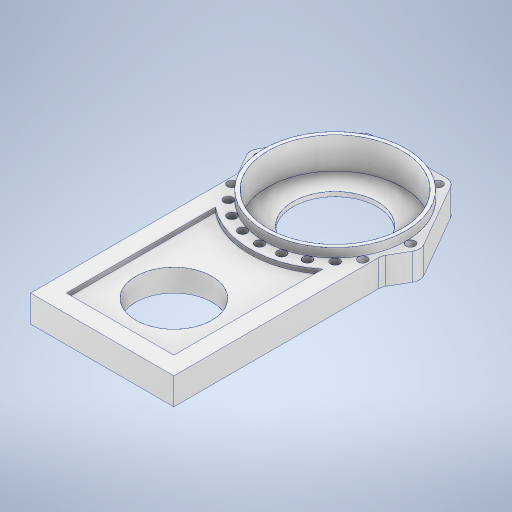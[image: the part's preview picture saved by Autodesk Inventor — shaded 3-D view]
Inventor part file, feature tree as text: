
AUTODESK INVENTOR PART (.ipt)
format: ipt  version: 2024 (Build 280153000, 153)  size: 427,520 bytes
history: native  units: mm
features: extrude x9, sketch x9, fillet x1, projected_geometry x1
ambient origin geometry x8: Origin, YZ Plane, XZ Plane, XY Plane, X Axis, Y Axis, Z Axis, Center Point
bodies: Solid1 (feature_tree)
feature tree (20):
  extrude  "Extrusion1"  Depth=160.0mm
  extrude  "Extrusion2"  Depth=30.0mm TaperAngle=0.0deg
  sketch  "Sketch3"  dims[d5=150.0mm d6=40.0mm d7=0.0mm]
  extrude  "Extrusion3"  Depth=40.0mm TaperAngle=0.0deg
  extrude  "Extrusion4"  Depth=10.0mm
  extrude  "Extrusion5"  Depth=5.0mm TaperAngle=0.0deg
  fillet  "Fillet1"  Radius=60.0mm
  extrude  "Extrusion6"  Depth=30.0mm TaperAngle=0.0deg
  extrude  "Extrusion7"  Depth=12.0mm
  extrude  "Extrusion8"  Depth=20.0mm
  extrude  "Extrusion9"  Depth=40.0mm
  sketch  "Sketch1"  dims[d0=250.0mm d1=160.0mm]
  sketch  "Sketch2"  dims[d2=160.0mm d3=30.0mm d4=0.0mm]
  sketch  "Sketch4"  dims[d8=10.0mm d9=94.0mm]
  sketch  "Sketch5"  dims[d10=150.0mm d11=5.0mm d12=0.0mm d13=60.0mm d15=360.0deg]
  sketch  "Sketch6"  dims[d18=60.0mm d19=360.0deg d20=30.0mm d21=0.0mm]
  projected_geometry  "Projected Loop1"
  sketch  "Sketch7"  dims[d22=30.0mm d23=0.0mm d24=12.0mm]
  sketch  "Sketch8"  dims[d25=20.0mm d26=190.0mm]
  sketch  "Sketch9"  dims[d27=5.0mm d28=0.0mm d29=150.0mm d30=10.0mm d31=0.0mm d32=84.286mm d33=240.0mm d35=360.0deg d37=35.0mm d38=0.0mm d39=10.0mm d40=85.0mm d41=40.0mm d42=0.0mm d17=0.5mm]
